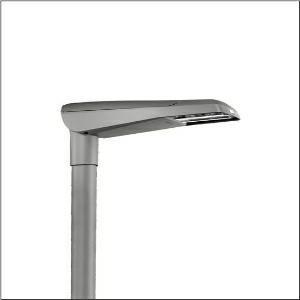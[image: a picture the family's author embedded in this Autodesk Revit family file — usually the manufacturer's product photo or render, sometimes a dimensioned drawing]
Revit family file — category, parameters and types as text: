
# Revit family: streetlight_sl_11_iq_micro___st1_0a_5xc1m41f08ce_367f
name_source: partatom
category: Lighting Fixtures
units: mm (PartAtom-declared; Revit-internal decimal feet)

## family parameters
Cut with Voids When Loaded = No
Host = Face
Light Source = No
Part Type = Normal
Room Calculation Point = No
Round Connector Dimension = Use Diameter
Shared = No

## types (1)
- --- (1 x LED, 1890 lm, 12.6 W, 4000K)
    Apparent Load = 13 VA
    CIE Flux Codes = 33 66 96 100 100
    Color Rendering = 70
    Color Temperature = 4000K
    Default Elevation = 1800 mm
    Description = Streetlight SL 11 iQ micro, mast luminaire, primary light control with 3 zone facetted reflector, of plastic, silver coated, highly specular, primary optical cover: cover, of PMMA, transparent, light distribution: ST1.0a, light emission: direct distribution, primary light characteristic: asymmetric, installation type: post-top, side-entry, lamps: LED, High Power LED, rated values: 1.890lm | 12,6W | 150lm/W (begin service life); end service life: 1.890lm | 12,9W; at 50% lumin. flux: 945lm | 6,8W | 139lm/W, colour temperature: 4000K, colour rendering: CRI > 70, light colour: 740, light setting 1 begin service life: 100% | 1.890lm | 12,6W | 150lm/W | 4.000K, light setting 1 end service life: 12,9W, further light settings possible, control: optimised constant luminous flux control (CLO 2.0), Desk-Remote (wireless, voltage-free reading and setting of iQ features in the workshop via application-optimized NFC function/RFID function), Light-Fading, Smart-Wire, Night-Set, Lumen-Switch, Temp-Guard, Auto-Match, Street-Remote, with cable H07RN-F 3x 1.5mm², mains connection: 230..240V, AC, 50/60Hz, connection cable pre-assembled, cable length: 5,5m, luminaire housing, of diecast aluminium, powder-coated, SITECO metallic grey (DB 702S), please order mast flange separately, inclination adjustable without tools: 0°, 5°, 10°, 15° (post-top) | 0°, -5°, -10°, -15° (side-entry), sealing non-destructively replaceable, multi-level sealing system, length: 600mm, width: 174mm, height: 116mm, mast flange for spigot size: 42mm (side-entry): 5XC10008XM4, 60/48mm (side-entry/post-top): 5XC10108XM2, 76/60mm (side-entry/post-top): 5XC10108XM1, equipment: standard, protection rating (complete): IP66, insulation class (complete): insulation class II (safety insulation), certification: CE, ENEC, ENEC+, VDE, impact resistance: IK10, permissible operating ambient temperature for outdoor applications: -25..+50°C, standard-compliant lighting for roads and squares, Environmental Product Declaration (EPD) tested and certified by an independent institute, packaging unit: 1 piece

Light Distribution: ST1.0a
    Height = 116 mm
    Lamp = 1 x LED
    Lamp Light Flux = 1890 lm
    Lamp Power = 12.6 W
    Lamp count = 1
    Length = 600 mm
    Luminous efficacy = 150 lm/W
    Manufacturer = Siteco
    ModVariant = No
    Model = 5XC1M41F08CE
    Number of Poles = 1
    OnlyDefault = Yes
    Power Factor = 1
    Product Name = Streetlight SL 11 iQ micro | ST1.0a
    Product group = mast luminaire | pylon top
    ProductGroupID = 6100
    Protection Class = Protection class II
    Protection Degree = IP 66
    RLX_Detail_Level = 1
    RLX_Emergency_Light_Flux = 0 lm
    RLX_Emergency_Type = 0
    RLX_Emergency_Type_DB = No
    RlxData = <blob elided: 26281 chars, md5=ea19ad00>
    Socket = socket
    Standby Power = 0 W
    System Light Flux = 1890 lm
    System Power = 13 W
    Type Comments = factory setting: luminous flux: 100 % | dim-lin: 254 | 229 mA
    Type Image = l_1006566.jpg
    URL = http://relux.com
    VarID = @adj_021593
    Voltage = 0 V
    Weight = 0.00 kg
    Width = 174 mm

## geometry (parser evidence)
native form markers: Blend x4, Sweep x9
no freeform markers — native parametric forms only
